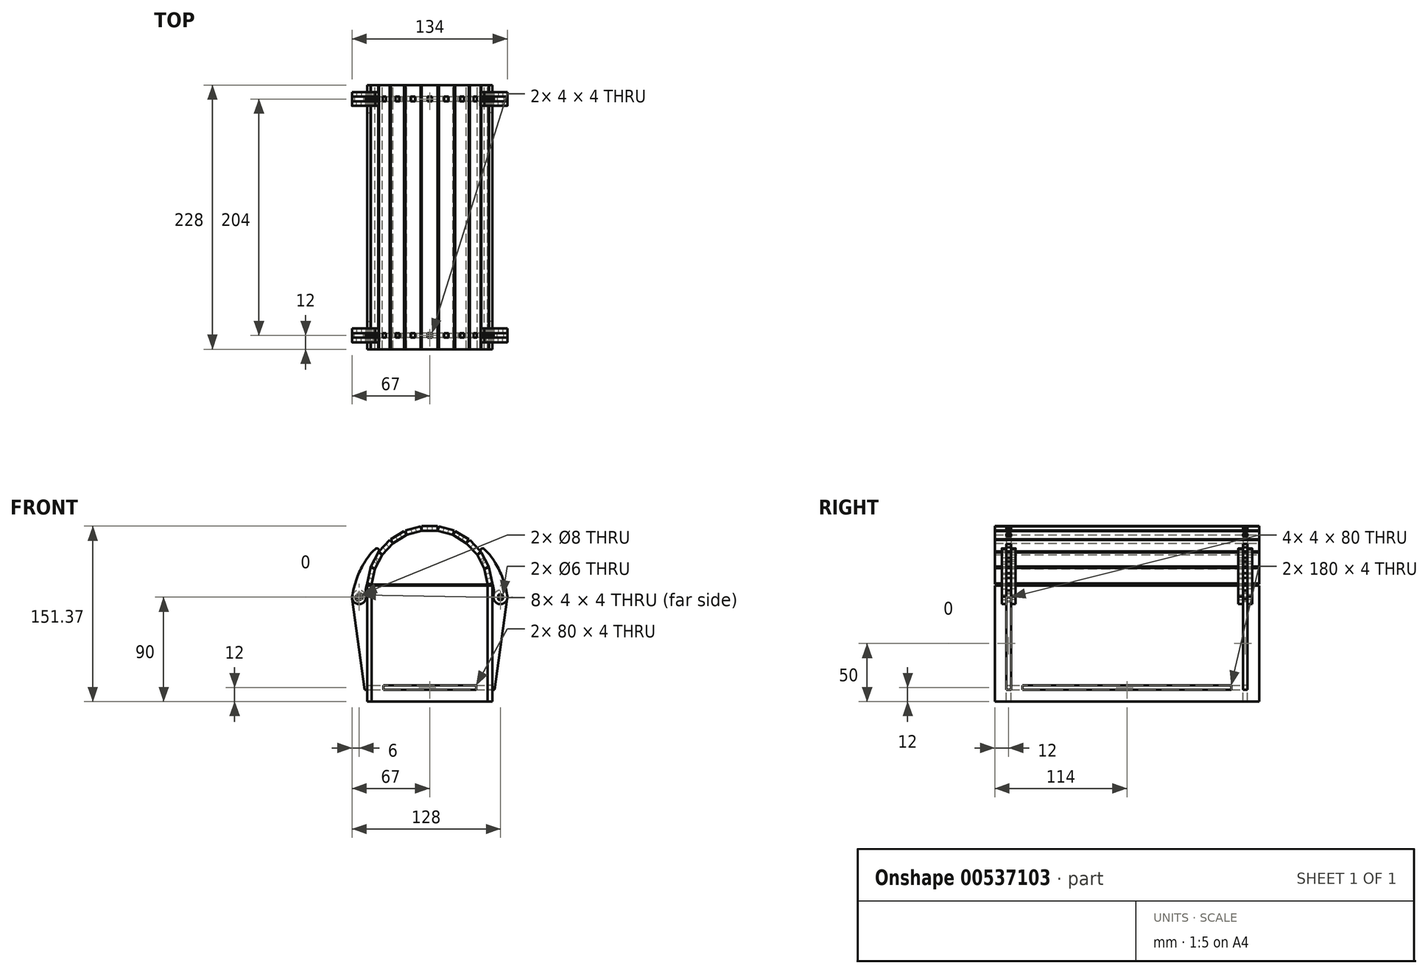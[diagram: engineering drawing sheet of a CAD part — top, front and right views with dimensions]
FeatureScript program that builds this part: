
annotation { "Feature Type Name" : "Feature", "Feature Type Description" : "" }
export const myFeature = defineFeature(function(context is Context, id is Id, definition is map)
    precondition{}
    {
        {
            var Q0;
            Q0=qCreatedBy(makeId("Front.planeOp"),FACE);
            cPlane(context, id + "F0", {"entities" : qUnion([Q0]), "cplaneType" : CPlaneType.OFFSET, "offset" : 100 * mm, "width" : 150 * mm, "height" : 150 * mm});
        }
        {
            var Q0;
            Q0=qCreatedBy(makeId("Front.planeOp"),FACE);
            cPlane(context, id + "F1", {"entities" : qUnion([Q0]), "cplaneType" : CPlaneType.OFFSET, "offset" : 100 * mm, "oppositeDirection" : true, "width" : 150 * mm, "height" : 150 * mm});
        }
        {
            var Q0;
            Q0=qCreatedBy(makeId("Right.planeOp"),FACE);
            cPlane(context, id + "F2", {"entities" : qUnion([Q0]), "cplaneType" : CPlaneType.OFFSET, "offset" : 50 * mm, "width" : 150 * mm, "height" : 150 * mm});
        }
        {
            var Q0;
            Q0=qCreatedBy(makeId("Right.planeOp"),FACE);
            cPlane(context, id + "F3", {"entities" : qUnion([Q0]), "cplaneType" : CPlaneType.OFFSET, "offset" : 50 * mm, "oppositeDirection" : true, "width" : 150 * mm, "height" : 150 * mm});
        }
        {
            var Q0;
            Q0=qCreatedBy(makeId("Top.planeOp"),FACE);
            cPlane(context, id + "F4", {"entities" : qUnion([Q0]), "cplaneType" : CPlaneType.OFFSET, "offset" : 40 * mm, "oppositeDirection" : true, "width" : 150 * mm, "height" : 150 * mm});
        }
        {
            var Q0;
            Q0=qCreatedBy(id+"F0.planeOp",FACE);
            var sketch = newSketch(context, id + "F5", { "sketchPlane" : qUnion([Q0])});
            skLineSegment(sketch, "E0.bottom", {"start": v(50, -50) * mm, "end": v(-50, -50) * mm});
            skLineSegment(sketch, "E0.top", {"start": v(50, 50) * mm, "end": v(-50, 50) * mm});
            skLineSegment(sketch, "E0.left", {"start": v(50, -50) * mm, "end": v(50, -40) * mm});
            skLineSegment(sketch, "E0.right", {"start": v(-50, -50) * mm, "end": v(-50, -40) * mm});
            skPoint(sketch, "E0.middle", {"position": v(0, 0) * mm});
            skLineSegment(sketch, "E1.bottom", {"start": v(-40, -36) * mm, "end": v(40, -36) * mm});
            skLineSegment(sketch, "E1.top", {"start": v(-40, -40) * mm, "end": v(40, -40) * mm});
            skLineSegment(sketch, "E1.left", {"start": v(-40, -36) * mm, "end": v(-40, -40) * mm});
            skLineSegment(sketch, "E1.right", {"start": v(40, -36) * mm, "end": v(40, -40) * mm});
            skLineSegment(sketch, "E2.bottom", {"start": v(-55, 40) * mm, "end": v(-50, 40) * mm});
            skLineSegment(sketch, "E2.top", {"start": v(-56, -40) * mm, "end": v(-50, -40) * mm});
            skLineSegment(sketch, "E3.trimOffspring", {"start": v(50, 40) * mm, "end": v(50, 50) * mm});
            skLineSegment(sketch, "E4.trimOffspring", {"start": v(-50, 40) * mm, "end": v(-50, 50) * mm});
            skPoint(sketch, "E5", {"position": v(0, 50) * mm});
            skLineSegment(sketch, "E6", {"start": v(-2, 97.37) * mm, "end": v(-2, 101.37) * mm});
            skLineSegment(sketch, "E7", {"start": v(-2, 101.37) * mm, "end": v(2, 101.37) * mm});
            skLineSegment(sketch, "E8", {"start": v(2, 101.37) * mm, "end": v(2, 97.37) * mm});
            skLineSegment(sketch, "E9", {"start": v(2, 97.37) * mm, "end": v(6.82, 97.37) * mm});
            skLineSegment(sketch, "E10", {"start": v(-2, 97.37) * mm, "end": v(-6.82, 97.37) * mm});
            skLineSegment(sketch, "E11.1.0", {"start": v(-12.54, 99.92) * mm, "end": v(-11.46, 96.07) * mm});
            skLineSegment(sketch, "E11.1.1", {"start": v(-16.4, 98.85) * mm, "end": v(-12.54, 99.92) * mm});
            skLineSegment(sketch, "E11.1.2", {"start": v(-15.31, 95) * mm, "end": v(-16.4, 98.85) * mm});
            skLineSegment(sketch, "E11.1.3", {"start": v(-15.31, 95) * mm, "end": v(-19.95, 93.7) * mm});
            skLineSegment(sketch, "E11.1.4", {"start": v(-11.46, 96.07) * mm, "end": v(-6.82, 97.37) * mm});
            skLineSegment(sketch, "E11.2.0", {"start": v(-26.15, 94.6) * mm, "end": v(-24.07, 91.19) * mm});
            skLineSegment(sketch, "E11.2.1", {"start": v(-29.57, 92.53) * mm, "end": v(-26.15, 94.6) * mm});
            skLineSegment(sketch, "E11.2.2", {"start": v(-27.49, 89.11) * mm, "end": v(-29.57, 92.53) * mm});
            skLineSegment(sketch, "E11.2.3", {"start": v(-27.49, 89.11) * mm, "end": v(-31.6, 86.6) * mm});
            skLineSegment(sketch, "E11.2.4", {"start": v(-24.07, 91.19) * mm, "end": v(-19.95, 93.7) * mm});
            skLineSegment(sketch, "E11.3.0", {"start": v(-37.82, 85.82) * mm, "end": v(-34.9, 83.08) * mm});
            skLineSegment(sketch, "E11.3.1", {"start": v(-40.55, 82.9) * mm, "end": v(-37.82, 85.82) * mm});
            skLineSegment(sketch, "E11.3.2", {"start": v(-37.62, 80.16) * mm, "end": v(-40.55, 82.9) * mm});
            skLineSegment(sketch, "E11.3.3", {"start": v(-37.62, 80.16) * mm, "end": v(-40.91, 76.64) * mm});
            skLineSegment(sketch, "E11.3.4", {"start": v(-34.9, 83.08) * mm, "end": v(-31.6, 86.6) * mm});
            skLineSegment(sketch, "E11.4.0", {"start": v(-46.68, 74.2) * mm, "end": v(-43.13, 72.36) * mm});
            skLineSegment(sketch, "E11.4.1", {"start": v(-48.52, 70.65) * mm, "end": v(-46.68, 74.2) * mm});
            skLineSegment(sketch, "E11.4.2", {"start": v(-44.97, 68.8) * mm, "end": v(-48.52, 70.65) * mm});
            skLineSegment(sketch, "E11.4.3", {"start": v(-44.97, 68.8) * mm, "end": v(-47.19, 64.53) * mm});
            skLineSegment(sketch, "E11.4.4", {"start": v(-43.13, 72.36) * mm, "end": v(-40.91, 76.64) * mm});
            skLineSegment(sketch, "E11.5.0", {"start": v(-52.09, 60.63) * mm, "end": v(-48.17, 59.81) * mm});
            skLineSegment(sketch, "E11.5.1", {"start": v(-52.9, 56.7) * mm, "end": v(-52.09, 60.63) * mm});
            skLineSegment(sketch, "E11.5.2", {"start": v(-48.98, 55.9) * mm, "end": v(-52.9, 56.7) * mm});
            skLineSegment(sketch, "E11.5.3", {"start": v(-48.98, 55.9) * mm, "end": v(-50, 51) * mm});
            skLineSegment(sketch, "E11.5.4", {"start": v(-48.17, 59.81) * mm, "end": v(-47.19, 64.53) * mm});
            skLineSegment(sketch, "E11.18.0", {"start": v(52.9, 56.7) * mm, "end": v(48.98, 55.9) * mm});
            skLineSegment(sketch, "E11.18.1", {"start": v(52.09, 60.63) * mm, "end": v(52.9, 56.7) * mm});
            skLineSegment(sketch, "E11.18.2", {"start": v(48.17, 59.81) * mm, "end": v(52.09, 60.63) * mm});
            skLineSegment(sketch, "E11.18.3", {"start": v(48.17, 59.81) * mm, "end": v(47.19, 64.53) * mm});
            skLineSegment(sketch, "E11.18.4", {"start": v(48.98, 55.9) * mm, "end": v(50, 51) * mm});
            skLineSegment(sketch, "E11.19.0", {"start": v(48.52, 70.65) * mm, "end": v(44.97, 68.8) * mm});
            skLineSegment(sketch, "E11.19.1", {"start": v(46.68, 74.2) * mm, "end": v(48.52, 70.65) * mm});
            skLineSegment(sketch, "E11.19.2", {"start": v(43.13, 72.36) * mm, "end": v(46.68, 74.2) * mm});
            skLineSegment(sketch, "E11.19.3", {"start": v(43.13, 72.36) * mm, "end": v(40.91, 76.64) * mm});
            skLineSegment(sketch, "E11.19.4", {"start": v(44.97, 68.8) * mm, "end": v(47.19, 64.53) * mm});
            skLineSegment(sketch, "E11.20.0", {"start": v(40.55, 82.9) * mm, "end": v(37.62, 80.16) * mm});
            skLineSegment(sketch, "E11.20.1", {"start": v(37.82, 85.82) * mm, "end": v(40.55, 82.9) * mm});
            skLineSegment(sketch, "E11.20.2", {"start": v(34.9, 83.08) * mm, "end": v(37.82, 85.82) * mm});
            skLineSegment(sketch, "E11.20.3", {"start": v(34.9, 83.08) * mm, "end": v(31.6, 86.6) * mm});
            skLineSegment(sketch, "E11.20.4", {"start": v(37.62, 80.16) * mm, "end": v(40.91, 76.64) * mm});
            skLineSegment(sketch, "E11.21.0", {"start": v(29.57, 92.53) * mm, "end": v(27.49, 89.11) * mm});
            skLineSegment(sketch, "E11.21.1", {"start": v(26.15, 94.6) * mm, "end": v(29.57, 92.53) * mm});
            skLineSegment(sketch, "E11.21.2", {"start": v(24.07, 91.19) * mm, "end": v(26.15, 94.6) * mm});
            skLineSegment(sketch, "E11.21.3", {"start": v(24.07, 91.19) * mm, "end": v(19.95, 93.7) * mm});
            skLineSegment(sketch, "E11.21.4", {"start": v(27.49, 89.11) * mm, "end": v(31.6, 86.6) * mm});
            skLineSegment(sketch, "E11.22.0", {"start": v(16.4, 98.85) * mm, "end": v(15.31, 95) * mm});
            skLineSegment(sketch, "E11.22.1", {"start": v(12.54, 99.92) * mm, "end": v(16.4, 98.85) * mm});
            skLineSegment(sketch, "E11.22.2", {"start": v(11.46, 96.07) * mm, "end": v(12.54, 99.92) * mm});
            skLineSegment(sketch, "E11.22.3", {"start": v(11.46, 96.07) * mm, "end": v(6.82, 97.37) * mm});
            skLineSegment(sketch, "E11.22.4", {"start": v(15.31, 95) * mm, "end": v(19.95, 93.7) * mm});
            skLineSegment(sketch, "E12", {"start": v(50, 51) * mm, "end": v(-50, 51) * mm});
            skCircle(sketch, "E13", {"center": v(-61, 40) * mm, "radius": 4 * mm});
            skArc(sketch, "E14", {"start": v(-55, 40) * mm, "mid": v(-61.09, 46) * mm, "end": v(-67, 39.83) * mm});
            skLineSegment(sketch, "E15", {"start": v(-67, 39.83) * mm, "end": v(-56, -40) * mm});
            skPoint(sketch, "E16.end.orphan", {"position": v(-57, 40) * mm});
            skLineSegment(sketch, "E17.MirrorCS", {"start": v(67, 39.83) * mm, "end": v(56, -40) * mm});
            skLineSegment(sketch, "E18.MirrorCS", {"start": v(55, 40) * mm, "end": v(50, 40) * mm});
            skArc(sketch, "E19.MirrorCS", {"start": v(55, 40) * mm, "mid": v(61.09, 46) * mm, "end": v(67, 39.83) * mm});
            skLineSegment(sketch, "E20", {"start": v(40, -40) * mm, "end": v(56, -40) * mm});
            skCircle(sketch, "E21", {"center": v(61, 40) * mm, "radius": 3 * mm});
            skSolve(sketch);
        }
        {
            var Q0;
            Q0 = qSketchRegion(id + "F5", true);
            extrude(context, id + "F6", {"entities" : qUnion([Q0]), "depth" : 4 * mm, "offsetDistance" : 25 * mm});
        }
        {
            var Q0;
            Q0=qCreatedBy(id+"F1.planeOp",FACE);
            var sketch = newSketch(context, id + "F7", { "sketchPlane" : qUnion([Q0])});
            skLineSegment(sketch, "E22.bottom", {"start": v(50, -50) * mm, "end": v(-50, -50) * mm});
            skLineSegment(sketch, "E22.top", {"start": v(50, 50) * mm, "end": v(-50, 50) * mm});
            skLineSegment(sketch, "E22.left", {"start": v(50, -50) * mm, "end": v(50, -40) * mm});
            skLineSegment(sketch, "E22.right", {"start": v(-50, -50) * mm, "end": v(-50, -40) * mm});
            skPoint(sketch, "E22.middle", {"position": v(0, 0) * mm});
            skLineSegment(sketch, "E23.bottom", {"start": v(-40, -36) * mm, "end": v(40, -36) * mm});
            skLineSegment(sketch, "E23.top", {"start": v(-40, -40) * mm, "end": v(40, -40) * mm});
            skLineSegment(sketch, "E23.left", {"start": v(-40, -36) * mm, "end": v(-40, -40) * mm});
            skLineSegment(sketch, "E23.right", {"start": v(40, -36) * mm, "end": v(40, -40) * mm});
            skLineSegment(sketch, "E24.top", {"start": v(-56, -40) * mm, "end": v(-50, -40) * mm});
            skLineSegment(sketch, "E25.trimOffspring", {"start": v(50, 40) * mm, "end": v(50, 50) * mm});
            skLineSegment(sketch, "E26.trimOffspring", {"start": v(-50, 40) * mm, "end": v(-50, 50) * mm});
            skLineSegment(sketch, "E27.bottom", {"start": v(-55, 40) * mm, "end": v(-50, 40) * mm});
            skCircle(sketch, "E28", {"center": v(-61, 40) * mm, "radius": 4 * mm});
            skArc(sketch, "E29", {"start": v(-55, 40) * mm, "mid": v(-61.73, 45.95) * mm, "end": v(-66.82, 38.54) * mm});
            skLineSegment(sketch, "E30", {"start": v(-67, 39.83) * mm, "end": v(-56, -40) * mm});
            skLineSegment(sketch, "E31.MirrorCS", {"start": v(55, 40) * mm, "end": v(50, 40) * mm});
            skArc(sketch, "E32.MirrorCS", {"start": v(55, 40) * mm, "mid": v(61.73, 45.95) * mm, "end": v(66.82, 38.54) * mm});
            skLineSegment(sketch, "E33.MirrorCS", {"start": v(67, 39.83) * mm, "end": v(56, -40) * mm});
            skLineSegment(sketch, "E34.MirrorCS", {"start": v(56, -40) * mm, "end": v(50, -40) * mm});
            skCircle(sketch, "E35", {"center": v(61, 40) * mm, "radius": 3 * mm});
            skSolve(sketch);
        }
        {
            var Q0;
            Q0 = qSketchRegion(id + "F7", true);
            extrude(context, id + "F8", {"entities" : qUnion([Q0]), "oppositeDirection" : true, "depth" : 4 * mm, "offsetDistance" : 25 * mm});
        }
        {
            var Q0;
            Q0=qCreatedBy(id+"F2.planeOp",FACE);
            var sketch = newSketch(context, id + "F9", { "sketchPlane" : qUnion([Q0])});
            skLineSegment(sketch, "E36.bottom", {"start": v(-114, 50) * mm, "end": v(114, 50) * mm});
            skLineSegment(sketch, "E36.top", {"start": v(-114, -50) * mm, "end": v(114, -50) * mm});
            skLineSegment(sketch, "E36.left", {"start": v(-114, 50) * mm, "end": v(-114, -50) * mm});
            skLineSegment(sketch, "E36.right", {"start": v(114, 50) * mm, "end": v(114, -50) * mm});
            skPoint(sketch, "E36.middle", {"position": v(0, 0) * mm});
            skLineSegment(sketch, "E37.bottom", {"start": v(-104, 40) * mm, "end": v(-100, 40) * mm});
            skLineSegment(sketch, "E37.top", {"start": v(-104, -40) * mm, "end": v(-100, -40) * mm});
            skLineSegment(sketch, "E37.left", {"start": v(-104, 40) * mm, "end": v(-104, -40) * mm});
            skLineSegment(sketch, "E37.right", {"start": v(-100, 40) * mm, "end": v(-100, -40) * mm});
            skLineSegment(sketch, "E38.MirrorCS", {"start": v(104, -40) * mm, "end": v(100, -40) * mm});
            skLineSegment(sketch, "E39.MirrorCS", {"start": v(104, 40) * mm, "end": v(100, 40) * mm});
            skLineSegment(sketch, "E40.MirrorCS", {"start": v(100, 40) * mm, "end": v(100, -40) * mm});
            skLineSegment(sketch, "E41.MirrorCS", {"start": v(104, 40) * mm, "end": v(104, -40) * mm});
            skLineSegment(sketch, "E42.bottom", {"start": v(-90, -36) * mm, "end": v(90, -36) * mm});
            skLineSegment(sketch, "E42.top", {"start": v(-90, -40) * mm, "end": v(90, -40) * mm});
            skLineSegment(sketch, "E42.left", {"start": v(-90, -36) * mm, "end": v(-90, -40) * mm});
            skLineSegment(sketch, "E42.right", {"start": v(90, -36) * mm, "end": v(90, -40) * mm});
            skSolve(sketch);
        }
        {
            var Q0;
            Q0 = qSketchRegion(id + "F9", true);
            extrude(context, id + "F10", {"entities" : qUnion([Q0]), "depth" : 4 * mm, "offsetDistance" : 25 * mm});
        }
        {
            var Q0;
            Q0=qCreatedBy(id+"F3.planeOp",FACE);
            var sketch = newSketch(context, id + "F11", { "sketchPlane" : qUnion([Q0])});
            skLineSegment(sketch, "E43.bottom", {"start": v(-114, 50) * mm, "end": v(114, 50) * mm});
            skLineSegment(sketch, "E43.top", {"start": v(-114, -50) * mm, "end": v(114, -50) * mm});
            skLineSegment(sketch, "E43.left", {"start": v(-114, 50) * mm, "end": v(-114, -50) * mm});
            skLineSegment(sketch, "E43.right", {"start": v(114, 50) * mm, "end": v(114, -50) * mm});
            skPoint(sketch, "E43.middle", {"position": v(0, 0) * mm});
            skLineSegment(sketch, "E44.bottom", {"start": v(-104, 40) * mm, "end": v(-100, 40) * mm});
            skLineSegment(sketch, "E44.top", {"start": v(-104, -40) * mm, "end": v(-100, -40) * mm});
            skLineSegment(sketch, "E44.left", {"start": v(-104, 40) * mm, "end": v(-104, -40) * mm});
            skLineSegment(sketch, "E44.right", {"start": v(-100, 40) * mm, "end": v(-100, -40) * mm});
            skLineSegment(sketch, "E45.MirrorCS", {"start": v(104, -40) * mm, "end": v(100, -40) * mm});
            skLineSegment(sketch, "E46.MirrorCS", {"start": v(104, 40) * mm, "end": v(100, 40) * mm});
            skLineSegment(sketch, "E47.MirrorCS", {"start": v(100, 40) * mm, "end": v(100, -40) * mm});
            skLineSegment(sketch, "E48.MirrorCS", {"start": v(104, 40) * mm, "end": v(104, -40) * mm});
            skLineSegment(sketch, "E49.bottom", {"start": v(-90, -36) * mm, "end": v(90, -36) * mm});
            skLineSegment(sketch, "E49.top", {"start": v(-90, -40) * mm, "end": v(90, -40) * mm});
            skLineSegment(sketch, "E49.left", {"start": v(-90, -36) * mm, "end": v(-90, -40) * mm});
            skLineSegment(sketch, "E49.right", {"start": v(90, -36) * mm, "end": v(90, -40) * mm});
            skSolve(sketch);
        }
        {
            var Q0;
            Q0 = qSketchRegion(id + "F11", true);
            extrude(context, id + "F12", {"entities" : qUnion([Q0]), "oppositeDirection" : true, "depth" : 4 * mm, "offsetDistance" : 25 * mm});
        }
        {
            var Q0;
            Q0=qCreatedBy(id+"F4.planeOp",FACE);
            var sketch = newSketch(context, id + "F13", { "sketchPlane" : qUnion([Q0])});
            skLineSegment(sketch, "E50.bottom", {"start": v(-50, -100) * mm, "end": v(-40, -100) * mm});
            skLineSegment(sketch, "E50.top", {"start": v(-50, 100) * mm, "end": v(-40, 100) * mm});
            skLineSegment(sketch, "E50.left", {"start": v(-50, -100) * mm, "end": v(-50, -90) * mm});
            skLineSegment(sketch, "E50.right", {"start": v(50, -100) * mm, "end": v(50, -90) * mm});
            skPoint(sketch, "E50.middle", {"position": v(0, 0) * mm});
            skLineSegment(sketch, "E51.bottom", {"start": v(-54, -90) * mm, "end": v(-50, -90) * mm});
            skLineSegment(sketch, "E51.top", {"start": v(-54, 90) * mm, "end": v(-50, 90) * mm});
            skLineSegment(sketch, "E51.left", {"start": v(-54, -90) * mm, "end": v(-54, 90) * mm});
            skLineSegment(sketch, "E52.trimOffspring", {"start": v(-50, 90) * mm, "end": v(-50, 100) * mm});
            skLineSegment(sketch, "E53.MirrorCS", {"start": v(54, 90) * mm, "end": v(50, 90) * mm});
            skLineSegment(sketch, "E54.MirrorCS", {"start": v(54, -90) * mm, "end": v(50, -90) * mm});
            skLineSegment(sketch, "E55.MirrorCS", {"start": v(54, -90) * mm, "end": v(54, 90) * mm});
            skLineSegment(sketch, "E56.trimOffspring", {"start": v(50, 90) * mm, "end": v(50, 100) * mm});
            skLineSegment(sketch, "E57.bottom", {"start": v(40, -104) * mm, "end": v(-40, -104) * mm});
            skLineSegment(sketch, "E57.left", {"start": v(40, -104) * mm, "end": v(40, -100) * mm});
            skLineSegment(sketch, "E57.right", {"start": v(-40, -104) * mm, "end": v(-40, -100) * mm});
            skLineSegment(sketch, "E58", {"start": v(0, 0) * mm, "end": v(13.37, 0) * mm});
            skLineSegment(sketch, "E59.MirrorCS", {"start": v(-40, 104) * mm, "end": v(-40, 100) * mm});
            skLineSegment(sketch, "E60.MirrorCS", {"start": v(40, 104) * mm, "end": v(40, 100) * mm});
            skLineSegment(sketch, "E61.MirrorCS", {"start": v(40, 104) * mm, "end": v(-40, 104) * mm});
            skLineSegment(sketch, "E62.trimOffspring", {"start": v(40, -100) * mm, "end": v(50, -100) * mm});
            skLineSegment(sketch, "E63.trimOffspring", {"start": v(40, 100) * mm, "end": v(50, 100) * mm});
            skSolve(sketch);
        }
        {
            var Q0;
            Q0 = qSketchRegion(id + "F13", true);
            extrude(context, id + "F14", {"entities" : qUnion([Q0]), "depth" : 4 * mm, "offsetDistance" : 25 * mm});
        }
        {
            var Q0;
            Q0=makeQuery(id+"F6.opExtrude","SWEPT_BODY",BODY,{"disambiguationData":[OSD([sQuery(id+"F5.wireOp",EDGE,"E6"),sQuery(id+"F5.wireOp",EDGE,"E7"),sQuery(id+"F5.wireOp",EDGE,"E8"),sQuery(id+"F5.wireOp",EDGE,"E9"),sQuery(id+"F5.wireOp",EDGE,"E10"),sQuery(id+"F5.wireOp",EDGE,"E11.1.0"),sQuery(id+"F5.wireOp",EDGE,"E11.1.1"),sQuery(id+"F5.wireOp",EDGE,"E11.1.2"),sQuery(id+"F5.wireOp",EDGE,"E11.1.3"),sQuery(id+"F5.wireOp",EDGE,"E11.1.4"),sQuery(id+"F5.wireOp",EDGE,"E11.2.0"),sQuery(id+"F5.wireOp",EDGE,"E11.2.1"),sQuery(id+"F5.wireOp",EDGE,"E11.2.2"),sQuery(id+"F5.wireOp",EDGE,"E11.2.3"),sQuery(id+"F5.wireOp",EDGE,"E11.2.4"),sQuery(id+"F5.wireOp",EDGE,"E11.3.0"),sQuery(id+"F5.wireOp",EDGE,"E11.3.1"),sQuery(id+"F5.wireOp",EDGE,"E11.3.2"),sQuery(id+"F5.wireOp",EDGE,"E11.3.3"),sQuery(id+"F5.wireOp",EDGE,"E11.3.4"),sQuery(id+"F5.wireOp",EDGE,"E11.4.0"),sQuery(id+"F5.wireOp",EDGE,"E11.4.1"),sQuery(id+"F5.wireOp",EDGE,"E11.4.2"),sQuery(id+"F5.wireOp",EDGE,"E11.4.3"),sQuery(id+"F5.wireOp",EDGE,"E11.4.4"),sQuery(id+"F5.wireOp",EDGE,"E11.5.0"),sQuery(id+"F5.wireOp",EDGE,"E11.5.1"),sQuery(id+"F5.wireOp",EDGE,"E11.5.2"),sQuery(id+"F5.wireOp",EDGE,"E11.5.3"),sQuery(id+"F5.wireOp",EDGE,"E11.5.4"),sQuery(id+"F5.wireOp",EDGE,"E11.18.0"),sQuery(id+"F5.wireOp",EDGE,"E11.18.1"),sQuery(id+"F5.wireOp",EDGE,"E11.18.2"),sQuery(id+"F5.wireOp",EDGE,"E11.18.3"),sQuery(id+"F5.wireOp",EDGE,"E11.18.4"),sQuery(id+"F5.wireOp",EDGE,"E11.19.0"),sQuery(id+"F5.wireOp",EDGE,"E11.19.1"),sQuery(id+"F5.wireOp",EDGE,"E11.19.2"),sQuery(id+"F5.wireOp",EDGE,"E11.19.3"),sQuery(id+"F5.wireOp",EDGE,"E11.19.4"),sQuery(id+"F5.wireOp",EDGE,"E11.20.0"),sQuery(id+"F5.wireOp",EDGE,"E11.20.1"),sQuery(id+"F5.wireOp",EDGE,"E11.20.2"),sQuery(id+"F5.wireOp",EDGE,"E11.20.3"),sQuery(id+"F5.wireOp",EDGE,"E11.20.4"),sQuery(id+"F5.wireOp",EDGE,"E11.21.0"),sQuery(id+"F5.wireOp",EDGE,"E11.21.1"),sQuery(id+"F5.wireOp",EDGE,"E11.21.2"),sQuery(id+"F5.wireOp",EDGE,"E11.21.3"),sQuery(id+"F5.wireOp",EDGE,"E11.21.4"),sQuery(id+"F5.wireOp",EDGE,"E11.22.0"),sQuery(id+"F5.wireOp",EDGE,"E11.22.1"),sQuery(id+"F5.wireOp",EDGE,"E11.22.2"),sQuery(id+"F5.wireOp",EDGE,"E11.22.3"),sQuery(id+"F5.wireOp",EDGE,"E11.22.4"),sQuery(id+"F5.wireOp",EDGE,"E12")])]});
            var Q1;
            Q1=qCreatedBy(makeId("Front.planeOp"),FACE);
            mirror(context, id + "F15", {"entities" : qUnion([Q0]), "mirrorPlane" : qUnion([Q1])});
        }
        {
            var Q0;
            Q0=makeQuery(id+"F6.opExtrude","SWEPT_FACE",FACE,{"disambiguationData":[OSD([sQuery(id+"F5.wireOp",EDGE,"E9")])]});
            cPlane(context, id + "F16", {"entities" : qUnion([Q0]), "cplaneType" : CPlaneType.OFFSET, "offset" : 0 * mm, "width" : 150 * mm, "height" : 150 * mm});
        }
        {
            var Q0;
            Q0=qCreatedBy(id+"F16.planeOp",FACE);
            var sketch = newSketch(context, id + "F17", { "sketchPlane" : qUnion([Q0])});
            skLineSegment(sketch, "E64", {"start": v(-6.82, -114) * mm, "end": v(-6.82, 114) * mm});
            skLineSegment(sketch, "E65", {"start": v(6.82, -114) * mm, "end": v(6.82, 114) * mm});
            skLineSegment(sketch, "E66", {"start": v(-6.82, -114) * mm, "end": v(6.82, -114) * mm});
            skLineSegment(sketch, "E67.bottom", {"start": v(-2, -100) * mm, "end": v(2, -100) * mm});
            skLineSegment(sketch, "E67.top", {"start": v(-2, -104) * mm, "end": v(2, -104) * mm});
            skLineSegment(sketch, "E67.left", {"start": v(-2, -100) * mm, "end": v(-2, -104) * mm});
            skLineSegment(sketch, "E67.right", {"start": v(2, -100) * mm, "end": v(2, -104) * mm});
            skLineSegment(sketch, "E68.MirrorCS", {"start": v(-6.82, 114) * mm, "end": v(6.82, 114) * mm});
            skLineSegment(sketch, "E69.MirrorCS", {"start": v(2, 100) * mm, "end": v(2, 104) * mm});
            skLineSegment(sketch, "E70.MirrorCS", {"start": v(-2, 100) * mm, "end": v(2, 100) * mm});
            skLineSegment(sketch, "E71.MirrorCS", {"start": v(-2, 104) * mm, "end": v(2, 104) * mm});
            skLineSegment(sketch, "E72.MirrorCS", {"start": v(-2, 100) * mm, "end": v(-2, 104) * mm});
            skSolve(sketch);
        }
        {
            var Q0;
            Q0 = qSketchRegion(id + "F17", true);
            extrude(context, id + "F18", {"entities" : qUnion([Q0]), "depth" : 4 * mm, "offsetDistance" : 25 * mm});
        }
        {
            var Q0;
            Q0=makeQuery(id+"F6.opExtrude","SWEPT_FACE",FACE,{"disambiguationData":[OSD([sQuery(id+"F5.wireOp",EDGE,"E11.22.4")])]});
            cPlane(context, id + "F19", {"entities" : qUnion([Q0]), "cplaneType" : CPlaneType.OFFSET, "offset" : 0 * mm, "width" : 150 * mm, "height" : 150 * mm});
        }
        {
            var Q0;
            Q0=qCreatedBy(id+"F19.planeOp",FACE);
            var sketch = newSketch(context, id + "F20", { "sketchPlane" : qUnion([Q0])});
            skLineSegment(sketch, "E73", {"start": v(-19.7, -114) * mm, "end": v(-19.7, 114) * mm});
            skLineSegment(sketch, "E74", {"start": v(-6.07, -114) * mm, "end": v(-6.07, 114) * mm});
            skLineSegment(sketch, "E75", {"start": v(-19.7, -114) * mm, "end": v(-6.07, -114) * mm});
            skLineSegment(sketch, "E76.bottom", {"start": v(-14.89, -100) * mm, "end": v(-10.89, -100) * mm});
            skLineSegment(sketch, "E76.top", {"start": v(-14.89, -104) * mm, "end": v(-10.89, -104) * mm});
            skLineSegment(sketch, "E76.left", {"start": v(-14.89, -100) * mm, "end": v(-14.89, -104) * mm});
            skLineSegment(sketch, "E76.right", {"start": v(-10.89, -100) * mm, "end": v(-10.89, -104) * mm});
            skLineSegment(sketch, "E77.MirrorCS", {"start": v(-19.7, 114) * mm, "end": v(-6.07, 114) * mm});
            skLineSegment(sketch, "E78.MirrorCS", {"start": v(-10.89, 100) * mm, "end": v(-10.89, 104) * mm});
            skLineSegment(sketch, "E79.MirrorCS", {"start": v(-14.89, 100) * mm, "end": v(-10.89, 100) * mm});
            skLineSegment(sketch, "E80.MirrorCS", {"start": v(-14.89, 104) * mm, "end": v(-10.89, 104) * mm});
            skLineSegment(sketch, "E81.MirrorCS", {"start": v(-14.89, 100) * mm, "end": v(-14.89, 104) * mm});
            skSolve(sketch);
        }
        {
            var Q0;
            Q0 = qSketchRegion(id + "F20", true);
            extrude(context, id + "F21", {"entities" : qUnion([Q0]), "depth" : 4 * mm, "offsetDistance" : 25 * mm});
        }
        {
            var Q0;
            Q0=makeQuery(id+"F6.opExtrude","SWEPT_FACE",FACE,{"disambiguationData":[OSD([sQuery(id+"F5.wireOp",EDGE,"E11.21.4")])]});
            var sketch = newSketch(context, id + "F22", { "sketchPlane" : qUnion([Q0])});
            skLineSegment(sketch, "E82", {"start": v(-31.63, -114) * mm, "end": v(-31.63, 114) * mm});
            skLineSegment(sketch, "E83", {"start": v(-18, -114) * mm, "end": v(-18, 114) * mm});
            skLineSegment(sketch, "E84", {"start": v(-31.63, -114) * mm, "end": v(-18, -114) * mm});
            skLineSegment(sketch, "E85.bottom", {"start": v(-26.82, -100) * mm, "end": v(-22.82, -100) * mm});
            skLineSegment(sketch, "E85.top", {"start": v(-26.82, -104) * mm, "end": v(-22.82, -104) * mm});
            skLineSegment(sketch, "E85.left", {"start": v(-26.82, -100) * mm, "end": v(-26.82, -104) * mm});
            skLineSegment(sketch, "E85.right", {"start": v(-22.82, -100) * mm, "end": v(-22.82, -104) * mm});
            skLineSegment(sketch, "E86.MirrorCS", {"start": v(-31.63, 114) * mm, "end": v(-18, 114) * mm});
            skLineSegment(sketch, "E87.MirrorCS", {"start": v(-22.82, 100) * mm, "end": v(-22.82, 104) * mm});
            skLineSegment(sketch, "E88.MirrorCS", {"start": v(-26.82, 100) * mm, "end": v(-22.82, 100) * mm});
            skLineSegment(sketch, "E89.MirrorCS", {"start": v(-26.82, 104) * mm, "end": v(-22.82, 104) * mm});
            skLineSegment(sketch, "E90.MirrorCS", {"start": v(-26.82, 100) * mm, "end": v(-26.82, 104) * mm});
            skSolve(sketch);
        }
        {
            var Q0;
            Q0 = qSketchRegion(id + "F22", true);
            extrude(context, id + "F23", {"entities" : qUnion([Q0]), "depth" : 4 * mm, "offsetDistance" : 25 * mm});
        }
        {
            var Q0;
            Q0=makeQuery(id+"F6.opExtrude","SWEPT_FACE",FACE,{"disambiguationData":[OSD([sQuery(id+"F5.wireOp",EDGE,"E11.1.3")])]});
            var sketch = newSketch(context, id + "F24", { "sketchPlane" : qUnion([Q0])});
            skLineSegment(sketch, "E91", {"start": v(6.07, -114) * mm, "end": v(6.07, 114) * mm});
            skLineSegment(sketch, "E92", {"start": v(19.7, -114) * mm, "end": v(19.7, 114) * mm});
            skLineSegment(sketch, "E93", {"start": v(6.07, -114) * mm, "end": v(19.7, -114) * mm});
            skLineSegment(sketch, "E94.bottom", {"start": v(10.89, -100) * mm, "end": v(14.89, -100) * mm});
            skLineSegment(sketch, "E94.top", {"start": v(10.89, -104) * mm, "end": v(14.89, -104) * mm});
            skLineSegment(sketch, "E94.left", {"start": v(10.89, -100) * mm, "end": v(10.89, -104) * mm});
            skLineSegment(sketch, "E94.right", {"start": v(14.89, -100) * mm, "end": v(14.89, -104) * mm});
            skLineSegment(sketch, "E95.MirrorCS", {"start": v(6.07, 114) * mm, "end": v(19.7, 114) * mm});
            skLineSegment(sketch, "E96.MirrorCS", {"start": v(14.89, 100) * mm, "end": v(14.89, 104) * mm});
            skLineSegment(sketch, "E97.MirrorCS", {"start": v(10.89, 100) * mm, "end": v(14.89, 100) * mm});
            skLineSegment(sketch, "E98.MirrorCS", {"start": v(10.89, 104) * mm, "end": v(14.89, 104) * mm});
            skLineSegment(sketch, "E99.MirrorCS", {"start": v(10.89, 100) * mm, "end": v(10.89, 104) * mm});
            skSolve(sketch);
        }
        {
            var Q0;
            Q0 = qSketchRegion(id + "F24", true);
            extrude(context, id + "F25", {"entities" : qUnion([Q0]), "depth" : 4 * mm, "offsetDistance" : 25 * mm});
        }
        {
            var Q0;
            Q0=makeQuery(id+"F6.opExtrude","SWEPT_FACE",FACE,{"disambiguationData":[OSD([sQuery(id+"F5.wireOp",EDGE,"E11.2.3")])]});
            var sketch = newSketch(context, id + "F26", { "sketchPlane" : qUnion([Q0])});
            skLineSegment(sketch, "E100", {"start": v(18, -114) * mm, "end": v(18, 114) * mm});
            skLineSegment(sketch, "E101", {"start": v(31.63, -114) * mm, "end": v(31.63, 114) * mm});
            skLineSegment(sketch, "E102", {"start": v(18, -114) * mm, "end": v(31.63, -114) * mm});
            skLineSegment(sketch, "E103.bottom", {"start": v(22.82, -100) * mm, "end": v(26.82, -100) * mm});
            skLineSegment(sketch, "E103.top", {"start": v(22.82, -104) * mm, "end": v(26.82, -104) * mm});
            skLineSegment(sketch, "E103.left", {"start": v(22.82, -100) * mm, "end": v(22.82, -104) * mm});
            skLineSegment(sketch, "E103.right", {"start": v(26.82, -100) * mm, "end": v(26.82, -104) * mm});
            skLineSegment(sketch, "E104.MirrorCS", {"start": v(18, 114) * mm, "end": v(31.63, 114) * mm});
            skLineSegment(sketch, "E105.MirrorCS", {"start": v(26.82, 100) * mm, "end": v(26.82, 104) * mm});
            skLineSegment(sketch, "E106.MirrorCS", {"start": v(22.82, 100) * mm, "end": v(26.82, 100) * mm});
            skLineSegment(sketch, "E107.MirrorCS", {"start": v(22.82, 104) * mm, "end": v(26.82, 104) * mm});
            skLineSegment(sketch, "E108.MirrorCS", {"start": v(22.82, 100) * mm, "end": v(22.82, 104) * mm});
            skSolve(sketch);
        }
        {
            var Q0;
            Q0 = qSketchRegion(id + "F26", true);
            extrude(context, id + "F27", {"entities" : qUnion([Q0]), "depth" : 4 * mm, "offsetDistance" : 25 * mm});
        }
        {
            var Q0;
            Q0=makeQuery(id+"F6.opExtrude","SWEPT_FACE",FACE,{"disambiguationData":[OSD([sQuery(id+"F5.wireOp",EDGE,"E11.3.3")])]});
            var sketch = newSketch(context, id + "F28", { "sketchPlane" : qUnion([Q0])});
            skLineSegment(sketch, "E109", {"start": v(114, 28.09) * mm, "end": v(-114, 28.09) * mm});
            skLineSegment(sketch, "E110", {"start": v(114, 41.72) * mm, "end": v(-114, 41.72) * mm});
            skLineSegment(sketch, "E111", {"start": v(114, 28.09) * mm, "end": v(114, 41.72) * mm});
            skLineSegment(sketch, "E112.bottom", {"start": v(100, 32.9) * mm, "end": v(100, 36.9) * mm});
            skLineSegment(sketch, "E112.top", {"start": v(104, 32.9) * mm, "end": v(104, 36.9) * mm});
            skLineSegment(sketch, "E112.left", {"start": v(100, 32.9) * mm, "end": v(104, 32.9) * mm});
            skLineSegment(sketch, "E112.right", {"start": v(100, 36.9) * mm, "end": v(104, 36.9) * mm});
            skLineSegment(sketch, "E113.MirrorCS", {"start": v(-114, 28.09) * mm, "end": v(-114, 41.72) * mm});
            skLineSegment(sketch, "E114.MirrorCS", {"start": v(-100, 36.9) * mm, "end": v(-104, 36.9) * mm});
            skLineSegment(sketch, "E115.MirrorCS", {"start": v(-100, 32.9) * mm, "end": v(-100, 36.9) * mm});
            skLineSegment(sketch, "E116.MirrorCS", {"start": v(-104, 32.9) * mm, "end": v(-104, 36.9) * mm});
            skLineSegment(sketch, "E117.MirrorCS", {"start": v(-100, 32.9) * mm, "end": v(-104, 32.9) * mm});
            skSolve(sketch);
        }
        {
            var Q0;
            Q0 = qSketchRegion(id + "F28", true);
            extrude(context, id + "F29", {"entities" : qUnion([Q0]), "depth" : 4 * mm, "offsetDistance" : 25 * mm});
        }
        {
            var Q0;
            Q0=makeQuery(id+"F6.opExtrude","SWEPT_FACE",FACE,{"disambiguationData":[OSD([sQuery(id+"F5.wireOp",EDGE,"E11.4.3")])]});
            var sketch = newSketch(context, id + "F30", { "sketchPlane" : qUnion([Q0])});
            skLineSegment(sketch, "E118", {"start": v(114, 35.59) * mm, "end": v(-114, 35.59) * mm});
            skLineSegment(sketch, "E119", {"start": v(114, 49.22) * mm, "end": v(-114, 49.22) * mm});
            skLineSegment(sketch, "E120", {"start": v(114, 35.59) * mm, "end": v(114, 49.22) * mm});
            skLineSegment(sketch, "E121.bottom", {"start": v(100, 40.4) * mm, "end": v(100, 44.4) * mm});
            skLineSegment(sketch, "E121.top", {"start": v(108, 40.4) * mm, "end": v(108, 44.4) * mm});
            skLineSegment(sketch, "E121.left", {"start": v(100, 40.4) * mm, "end": v(108, 40.4) * mm});
            skLineSegment(sketch, "E121.right", {"start": v(100, 44.4) * mm, "end": v(108, 44.4) * mm});
            skLineSegment(sketch, "E122.MirrorCS", {"start": v(-114, 35.59) * mm, "end": v(-114, 49.22) * mm});
            skLineSegment(sketch, "E123.MirrorCS", {"start": v(-100, 44.4) * mm, "end": v(-108, 44.4) * mm});
            skLineSegment(sketch, "E124.MirrorCS", {"start": v(-100, 40.4) * mm, "end": v(-100, 44.4) * mm});
            skLineSegment(sketch, "E125.MirrorCS", {"start": v(-108, 40.4) * mm, "end": v(-108, 44.4) * mm});
            skLineSegment(sketch, "E126.MirrorCS", {"start": v(-100, 40.4) * mm, "end": v(-108, 40.4) * mm});
            skSolve(sketch);
        }
        {
            var Q0;
            Q0 = qSketchRegion(id + "F30", true);
            extrude(context, id + "F31", {"entities" : qUnion([Q0]), "depth" : 4 * mm, "offsetDistance" : 25 * mm});
        }
        {
            var Q0;
            Q0=makeQuery(id+"F6.opExtrude","SWEPT_FACE",FACE,{"disambiguationData":[OSD([sQuery(id+"F5.wireOp",EDGE,"E11.5.3")])]});
            var sketch = newSketch(context, id + "F32", { "sketchPlane" : qUnion([Q0])});
            skLineSegment(sketch, "E127", {"start": v(114, 39.94) * mm, "end": v(-114, 39.94) * mm});
            skLineSegment(sketch, "E128", {"start": v(114, 53.58) * mm, "end": v(-114, 53.58) * mm});
            skLineSegment(sketch, "E129", {"start": v(114, 39.94) * mm, "end": v(114, 53.58) * mm});
            skLineSegment(sketch, "E130.bottom", {"start": v(96, 44.76) * mm, "end": v(96, 48.76) * mm});
            skLineSegment(sketch, "E130.top", {"start": v(108, 44.76) * mm, "end": v(108, 48.76) * mm});
            skLineSegment(sketch, "E130.left", {"start": v(96, 44.76) * mm, "end": v(108, 44.76) * mm});
            skLineSegment(sketch, "E130.right", {"start": v(96, 48.76) * mm, "end": v(108, 48.76) * mm});
            skLineSegment(sketch, "E131.MirrorCS", {"start": v(-114, 39.94) * mm, "end": v(-114, 53.58) * mm});
            skLineSegment(sketch, "E132.bottom", {"start": v(-108, 48.76) * mm, "end": v(-96, 48.76) * mm});
            skLineSegment(sketch, "E132.top", {"start": v(-108, 44.76) * mm, "end": v(-96, 44.76) * mm});
            skLineSegment(sketch, "E132.left", {"start": v(-108, 48.76) * mm, "end": v(-108, 44.76) * mm});
            skLineSegment(sketch, "E132.right", {"start": v(-96, 48.76) * mm, "end": v(-96, 44.76) * mm});
            skSolve(sketch);
        }
        {
            var Q0;
            Q0 = qSketchRegion(id + "F32", true);
            extrude(context, id + "F33", {"entities" : qUnion([Q0]), "depth" : 4 * mm, "offsetDistance" : 25 * mm});
        }
        {
            var Q0;
            Q0=makeQuery(id+"F6.opExtrude","SWEPT_FACE",FACE,{"disambiguationData":[OSD([sQuery(id+"F5.wireOp",EDGE,"E11.20.4")])]});
            var sketch = newSketch(context, id + "F34", { "sketchPlane" : qUnion([Q0])});
            skLineSegment(sketch, "E133", {"start": v(-114, 41.72) * mm, "end": v(114, 41.72) * mm});
            skLineSegment(sketch, "E134", {"start": v(-114, 28.09) * mm, "end": v(114, 28.09) * mm});
            skLineSegment(sketch, "E135", {"start": v(-114, 41.72) * mm, "end": v(-114, 28.09) * mm});
            skLineSegment(sketch, "E136.bottom", {"start": v(-100, 36.9) * mm, "end": v(-100, 32.9) * mm});
            skLineSegment(sketch, "E136.top", {"start": v(-104, 36.9) * mm, "end": v(-104, 32.9) * mm});
            skLineSegment(sketch, "E136.left", {"start": v(-100, 36.9) * mm, "end": v(-104, 36.9) * mm});
            skLineSegment(sketch, "E136.right", {"start": v(-100, 32.9) * mm, "end": v(-104, 32.9) * mm});
            skLineSegment(sketch, "E137.MirrorCS", {"start": v(114, 41.72) * mm, "end": v(114, 28.09) * mm});
            skLineSegment(sketch, "E138.MirrorCS", {"start": v(100, 32.9) * mm, "end": v(104, 32.9) * mm});
            skLineSegment(sketch, "E139.MirrorCS", {"start": v(100, 36.9) * mm, "end": v(100, 32.9) * mm});
            skLineSegment(sketch, "E140.MirrorCS", {"start": v(104, 36.9) * mm, "end": v(104, 32.9) * mm});
            skLineSegment(sketch, "E141.MirrorCS", {"start": v(100, 36.9) * mm, "end": v(104, 36.9) * mm});
            skSolve(sketch);
        }
        {
            var Q0;
            Q0 = qSketchRegion(id + "F34", true);
            extrude(context, id + "F35", {"entities" : qUnion([Q0]), "depth" : 4 * mm, "offsetDistance" : 25 * mm});
        }
        {
            var Q0;
            Q0=makeQuery(id+"F6.opExtrude","SWEPT_FACE",FACE,{"disambiguationData":[OSD([sQuery(id+"F5.wireOp",EDGE,"E11.19.4")])]});
            var sketch = newSketch(context, id + "F36", { "sketchPlane" : qUnion([Q0])});
            skLineSegment(sketch, "E142", {"start": v(-114, 49.22) * mm, "end": v(114, 49.22) * mm});
            skLineSegment(sketch, "E143", {"start": v(-114, 35.59) * mm, "end": v(114, 35.59) * mm});
            skLineSegment(sketch, "E144", {"start": v(-114, 49.22) * mm, "end": v(-114, 35.59) * mm});
            skLineSegment(sketch, "E145.bottom", {"start": v(-96, 44.4) * mm, "end": v(-96, 40.4) * mm});
            skLineSegment(sketch, "E145.top", {"start": v(-108, 44.4) * mm, "end": v(-108, 40.4) * mm});
            skLineSegment(sketch, "E145.left", {"start": v(-96, 44.4) * mm, "end": v(-108, 44.4) * mm});
            skLineSegment(sketch, "E145.right", {"start": v(-96, 40.4) * mm, "end": v(-108, 40.4) * mm});
            skLineSegment(sketch, "E146.MirrorCS", {"start": v(114, 49.22) * mm, "end": v(114, 35.59) * mm});
            skLineSegment(sketch, "E147.MirrorCS", {"start": v(96, 40.4) * mm, "end": v(108, 40.4) * mm});
            skLineSegment(sketch, "E148.MirrorCS", {"start": v(96, 44.4) * mm, "end": v(108, 44.4) * mm});
            skLineSegment(sketch, "E149.MirrorCS", {"start": v(96, 44.4) * mm, "end": v(96, 40.4) * mm});
            skLineSegment(sketch, "E150.MirrorCS", {"start": v(108, 44.4) * mm, "end": v(108, 40.4) * mm});
            skSolve(sketch);
        }
        {
            var Q0;
            Q0 = qSketchRegion(id + "F36", true);
            extrude(context, id + "F37", {"entities" : qUnion([Q0]), "depth" : 4 * mm, "offsetDistance" : 25 * mm});
        }
        {
            var Q0;
            Q0=makeQuery(id+"F6.opExtrude","SWEPT_FACE",FACE,{"disambiguationData":[OSD([sQuery(id+"F5.wireOp",EDGE,"E11.18.4")])]});
            var sketch = newSketch(context, id + "F38", { "sketchPlane" : qUnion([Q0])});
            skLineSegment(sketch, "E151", {"start": v(-114, 53.58) * mm, "end": v(114, 53.58) * mm});
            skLineSegment(sketch, "E152", {"start": v(-114, 39.94) * mm, "end": v(114, 39.94) * mm});
            skLineSegment(sketch, "E153", {"start": v(-114, 53.58) * mm, "end": v(-114, 39.94) * mm});
            skLineSegment(sketch, "E154.bottom", {"start": v(-96, 48.76) * mm, "end": v(-96, 44.76) * mm});
            skLineSegment(sketch, "E154.top", {"start": v(-108, 48.76) * mm, "end": v(-108, 44.76) * mm});
            skLineSegment(sketch, "E154.right", {"start": v(-96, 44.76) * mm, "end": v(-108, 44.76) * mm});
            skLineSegment(sketch, "E155.MirrorCS", {"start": v(114, 53.58) * mm, "end": v(114, 39.94) * mm});
            skLineSegment(sketch, "E156.MirrorCS", {"start": v(96, 44.76) * mm, "end": v(108, 44.76) * mm});
            skLineSegment(sketch, "E157.MirrorCS", {"start": v(108, 48.76) * mm, "end": v(108, 44.76) * mm});
            skLineSegment(sketch, "E158.MirrorCS", {"start": v(96, 48.76) * mm, "end": v(96, 44.76) * mm});
            skLineSegment(sketch, "E159", {"start": v(-108, 48.76) * mm, "end": v(-96, 48.76) * mm});
            skLineSegment(sketch, "E160", {"start": v(96, 48.76) * mm, "end": v(108, 48.76) * mm});
            skSolve(sketch);
        }
        {
            var Q0;
            Q0 = qSketchRegion(id + "F38", true);
            extrude(context, id + "F39", {"entities" : qUnion([Q0]), "depth" : 4 * mm, "offsetDistance" : 25 * mm});
        }
        {
            var Q0;
            Q0=makeQuery(id+"F6.opExtrude","CAP_FACE",FACE,{"disambiguationData":[OSD([sQuery(id+"F5.wireOp",EDGE,"E6"),sQuery(id+"F5.wireOp",EDGE,"E7"),sQuery(id+"F5.wireOp",EDGE,"E8"),sQuery(id+"F5.wireOp",EDGE,"E9"),sQuery(id+"F5.wireOp",EDGE,"E10"),sQuery(id+"F5.wireOp",EDGE,"E11.1.0"),sQuery(id+"F5.wireOp",EDGE,"E11.1.1"),sQuery(id+"F5.wireOp",EDGE,"E11.1.2"),sQuery(id+"F5.wireOp",EDGE,"E11.1.3"),sQuery(id+"F5.wireOp",EDGE,"E11.1.4"),sQuery(id+"F5.wireOp",EDGE,"E11.2.0"),sQuery(id+"F5.wireOp",EDGE,"E11.2.1"),sQuery(id+"F5.wireOp",EDGE,"E11.2.2"),sQuery(id+"F5.wireOp",EDGE,"E11.2.3"),sQuery(id+"F5.wireOp",EDGE,"E11.2.4"),sQuery(id+"F5.wireOp",EDGE,"E11.3.0"),sQuery(id+"F5.wireOp",EDGE,"E11.3.1"),sQuery(id+"F5.wireOp",EDGE,"E11.3.2"),sQuery(id+"F5.wireOp",EDGE,"E11.3.3"),sQuery(id+"F5.wireOp",EDGE,"E11.3.4"),sQuery(id+"F5.wireOp",EDGE,"E11.4.0"),sQuery(id+"F5.wireOp",EDGE,"E11.4.1"),sQuery(id+"F5.wireOp",EDGE,"E11.4.2"),sQuery(id+"F5.wireOp",EDGE,"E11.4.3"),sQuery(id+"F5.wireOp",EDGE,"E11.4.4"),sQuery(id+"F5.wireOp",EDGE,"E11.5.0"),sQuery(id+"F5.wireOp",EDGE,"E11.5.1"),sQuery(id+"F5.wireOp",EDGE,"E11.5.2"),sQuery(id+"F5.wireOp",EDGE,"E11.5.3"),sQuery(id+"F5.wireOp",EDGE,"E11.5.4"),sQuery(id+"F5.wireOp",EDGE,"E11.18.0"),sQuery(id+"F5.wireOp",EDGE,"E11.18.1"),sQuery(id+"F5.wireOp",EDGE,"E11.18.2"),sQuery(id+"F5.wireOp",EDGE,"E11.18.3"),sQuery(id+"F5.wireOp",EDGE,"E11.18.4"),sQuery(id+"F5.wireOp",EDGE,"E11.19.0"),sQuery(id+"F5.wireOp",EDGE,"E11.19.1"),sQuery(id+"F5.wireOp",EDGE,"E11.19.2"),sQuery(id+"F5.wireOp",EDGE,"E11.19.3"),sQuery(id+"F5.wireOp",EDGE,"E11.19.4"),sQuery(id+"F5.wireOp",EDGE,"E11.20.0"),sQuery(id+"F5.wireOp",EDGE,"E11.20.1"),sQuery(id+"F5.wireOp",EDGE,"E11.20.2"),sQuery(id+"F5.wireOp",EDGE,"E11.20.3"),sQuery(id+"F5.wireOp",EDGE,"E11.20.4"),sQuery(id+"F5.wireOp",EDGE,"E11.21.0"),sQuery(id+"F5.wireOp",EDGE,"E11.21.1"),sQuery(id+"F5.wireOp",EDGE,"E11.21.2"),sQuery(id+"F5.wireOp",EDGE,"E11.21.3"),sQuery(id+"F5.wireOp",EDGE,"E11.21.4"),sQuery(id+"F5.wireOp",EDGE,"E11.22.0"),sQuery(id+"F5.wireOp",EDGE,"E11.22.1"),sQuery(id+"F5.wireOp",EDGE,"E11.22.2"),sQuery(id+"F5.wireOp",EDGE,"E11.22.3"),sQuery(id+"F5.wireOp",EDGE,"E11.22.4"),sQuery(id+"F5.wireOp",EDGE,"E12")])],"isStart":false});
            var sketch = newSketch(context, id + "F40", { "sketchPlane" : qUnion([Q0])});
            skCircle(sketch, "E161", {"center": v(-61, 40) * mm, "radius": 6 * mm});
            skLineSegment(sketch, "E162", {"start": v(-44.97, 68.8) * mm, "end": v(-48.52, 70.65) * mm});
            skLineSegment(sketch, "E163", {"start": v(-48.52, 70.65) * mm, "end": v(-51, 65.88) * mm});
            skLineSegment(sketch, "E164", {"start": v(-46.68, 74.2) * mm, "end": v(-43.97, 79.43) * mm});
            skArc(sketch, "E165.filletArc", {"start": v(-43.97, 79.43) * mm, "mid": v(-44.61, 81.85) * mm, "end": v(-47.09, 81.45) * mm});
            skLineSegment(sketch, "E166", {"start": v(-52.09, 60.63) * mm, "end": v(-51, 65.88) * mm});
            skLineSegment(sketch, "E167", {"start": v(-52.09, 60.63) * mm, "end": v(-48.17, 59.81) * mm});
            skLineSegment(sketch, "E168", {"start": v(-48.17, 59.81) * mm, "end": v(-48.98, 55.9) * mm});
            skLineSegment(sketch, "E169", {"start": v(-48.98, 55.9) * mm, "end": v(-52.9, 56.7) * mm});
            skLineSegment(sketch, "E170", {"start": v(-52.9, 56.7) * mm, "end": v(-53.88, 52) * mm});
            skLineSegment(sketch, "E171", {"start": v(-55, 39.89) * mm, "end": v(-55, 40.11) * mm});
            skLineSegment(sketch, "E172", {"start": v(-55, 40.11) * mm, "end": v(-55.13, 46.97) * mm});
            skFitSpline(sketch, "E173", {"points": [v(-53.88, 52) * mm, v(-54.53, 50.17) * mm, v(-55.13, 46.97) * mm, v(-55.13, 46.8) * mm, v(-55.13, 46.8) * mm], "startDerivative": vector(-1.69, -3.88) * mm, "endDerivative": vector(0, -0.06) * mm});
            skFitSpline(sketch, "E174", {"points": [v(-47.09, 81.45) * mm, v(-57.91, 67.12) * mm, v(-63.05, 55.7) * mm, v(-66.99, 40.35) * mm], "startDerivative": vector(-40.09, -32.55) * mm, "endDerivative": vector(-2.37, -33.03) * mm});
            skLineSegment(sketch, "E175.bottom", {"start": v(-63, 42) * mm, "end": v(-59, 42) * mm});
            skLineSegment(sketch, "E175.top", {"start": v(-63, 38) * mm, "end": v(-59, 38) * mm});
            skLineSegment(sketch, "E175.left", {"start": v(-63, 42) * mm, "end": v(-63, 38) * mm});
            skLineSegment(sketch, "E175.right", {"start": v(-59, 42) * mm, "end": v(-59, 38) * mm});
            skLineSegment(sketch, "E176", {"start": v(-46.68, 74.2) * mm, "end": v(-44.97, 68.8) * mm});
            skSolve(sketch);
        }
        {
            var Q0;
            Q0 = qSketchRegion(id + "F40", true);
            extrude(context, id + "F41", {"entities" : qUnion([Q0]), "depth" : 4 * mm, "offsetDistance" : 25 * mm});
        }
        {
            var Q0;
            Q0=makeQuery(id+"F41.opExtrude","SWEPT_BODY",BODY,{"disambiguationData":[OSD([sQuery(id+"F40.wireOp",EDGE,"E161"),sQuery(id+"F40.wireOp",EDGE,"t4tbokRh-8WQ7-ktuR-oRIJ-KhsfdOefVWlQ"),sQuery(id+"F40.wireOp",EDGE,"BNBL1Nzf-ZYxI-rDMI-PRVd-LXwGIi5Q9C7N"),sQuery(id+"F40.wireOp",EDGE,"E162"),sQuery(id+"F40.wireOp",EDGE,"E163"),sQuery(id+"F40.wireOp",EDGE,"E164"),sQuery(id+"F40.wireOp",EDGE,"E165.filletArc"),sQuery(id+"F40.wireOp",EDGE,"E166"),sQuery(id+"F40.wireOp",EDGE,"E167"),sQuery(id+"F40.wireOp",EDGE,"E168"),sQuery(id+"F40.wireOp",EDGE,"E169"),sQuery(id+"F40.wireOp",EDGE,"E170"),sQuery(id+"F40.wireOp",EDGE,"E172"),sQuery(id+"F40.wireOp",EDGE,"E173"),sQuery(id+"F40.wireOp",EDGE,"E174"),sQuery(id+"F40.wireOp",EDGE,"E175.bottom"),sQuery(id+"F40.wireOp",EDGE,"E175.top"),sQuery(id+"F40.wireOp",EDGE,"E175.left"),sQuery(id+"F40.wireOp",EDGE,"E175.right")])]});
            var Q1;
            Q1=qCreatedBy(makeId("Front.planeOp"),FACE);
            mirror(context, id + "F42", {"entities" : qUnion([Q0]), "mirrorPlane" : qUnion([Q1])});
        }
        {
            var Q0;
            Q0=makeQuery(id+"F41.opExtrude","SWEPT_BODY",BODY,{"disambiguationData":[OSD([sQuery(id+"F40.wireOp",EDGE,"E161"),sQuery(id+"F40.wireOp",EDGE,"t4tbokRh-8WQ7-ktuR-oRIJ-KhsfdOefVWlQ"),sQuery(id+"F40.wireOp",EDGE,"BNBL1Nzf-ZYxI-rDMI-PRVd-LXwGIi5Q9C7N"),sQuery(id+"F40.wireOp",EDGE,"E162"),sQuery(id+"F40.wireOp",EDGE,"E163"),sQuery(id+"F40.wireOp",EDGE,"E164"),sQuery(id+"F40.wireOp",EDGE,"E165.filletArc"),sQuery(id+"F40.wireOp",EDGE,"E166"),sQuery(id+"F40.wireOp",EDGE,"E167"),sQuery(id+"F40.wireOp",EDGE,"E168"),sQuery(id+"F40.wireOp",EDGE,"E169"),sQuery(id+"F40.wireOp",EDGE,"E170"),sQuery(id+"F40.wireOp",EDGE,"E172"),sQuery(id+"F40.wireOp",EDGE,"E173"),sQuery(id+"F40.wireOp",EDGE,"E174"),sQuery(id+"F40.wireOp",EDGE,"E175.bottom"),sQuery(id+"F40.wireOp",EDGE,"E175.top"),sQuery(id+"F40.wireOp",EDGE,"E175.left"),sQuery(id+"F40.wireOp",EDGE,"E175.right")])]});
            var Q1;
            Q1=qCreatedBy(id+"F0.planeOp",FACE);
            mirror(context, id + "F43", {"entities" : qUnion([Q0]), "mirrorPlane" : qUnion([Q1])});
        }
        {
            var Q0;
            Q0=makeQuery(id+"F43.opPattern","COPY",BODY,{"derivedFrom":makeQuery(id+"F41.opExtrude","SWEPT_BODY",BODY,{"disambiguationData":[OSD([sQuery(id+"F40.wireOp",EDGE,"E161"),sQuery(id+"F40.wireOp",EDGE,"t4tbokRh-8WQ7-ktuR-oRIJ-KhsfdOefVWlQ"),sQuery(id+"F40.wireOp",EDGE,"BNBL1Nzf-ZYxI-rDMI-PRVd-LXwGIi5Q9C7N"),sQuery(id+"F40.wireOp",EDGE,"E162"),sQuery(id+"F40.wireOp",EDGE,"E163"),sQuery(id+"F40.wireOp",EDGE,"E164"),sQuery(id+"F40.wireOp",EDGE,"E165.filletArc"),sQuery(id+"F40.wireOp",EDGE,"E166"),sQuery(id+"F40.wireOp",EDGE,"E167"),sQuery(id+"F40.wireOp",EDGE,"E168"),sQuery(id+"F40.wireOp",EDGE,"E169"),sQuery(id+"F40.wireOp",EDGE,"E170"),sQuery(id+"F40.wireOp",EDGE,"E172"),sQuery(id+"F40.wireOp",EDGE,"E173"),sQuery(id+"F40.wireOp",EDGE,"E174"),sQuery(id+"F40.wireOp",EDGE,"E175.bottom"),sQuery(id+"F40.wireOp",EDGE,"E175.top"),sQuery(id+"F40.wireOp",EDGE,"E175.left"),sQuery(id+"F40.wireOp",EDGE,"E175.right")])]}),"instanceName":"1"});
            transform(context, id + "F44", {"entities" : qUnion([Q0]), "transformType" : TransformType.TRANSLATION_3D, "dx" : 0 * mm, "dy" : -4 * mm, "dz" : 0 * mm, "makeCopy" : false});
        }
        {
            var Q0;
            Q0=makeQuery(id+"F43.opPattern","COPY",BODY,{"derivedFrom":makeQuery(id+"F41.opExtrude","SWEPT_BODY",BODY,{"disambiguationData":[OSD([sQuery(id+"F40.wireOp",EDGE,"E161"),sQuery(id+"F40.wireOp",EDGE,"t4tbokRh-8WQ7-ktuR-oRIJ-KhsfdOefVWlQ"),sQuery(id+"F40.wireOp",EDGE,"BNBL1Nzf-ZYxI-rDMI-PRVd-LXwGIi5Q9C7N"),sQuery(id+"F40.wireOp",EDGE,"E162"),sQuery(id+"F40.wireOp",EDGE,"E163"),sQuery(id+"F40.wireOp",EDGE,"E164"),sQuery(id+"F40.wireOp",EDGE,"E165.filletArc"),sQuery(id+"F40.wireOp",EDGE,"E166"),sQuery(id+"F40.wireOp",EDGE,"E167"),sQuery(id+"F40.wireOp",EDGE,"E168"),sQuery(id+"F40.wireOp",EDGE,"E169"),sQuery(id+"F40.wireOp",EDGE,"E170"),sQuery(id+"F40.wireOp",EDGE,"E172"),sQuery(id+"F40.wireOp",EDGE,"E173"),sQuery(id+"F40.wireOp",EDGE,"E174"),sQuery(id+"F40.wireOp",EDGE,"E175.bottom"),sQuery(id+"F40.wireOp",EDGE,"E175.top"),sQuery(id+"F40.wireOp",EDGE,"E175.left"),sQuery(id+"F40.wireOp",EDGE,"E175.right")])]}),"instanceName":"1"});
            var Q1;
            Q1=qCreatedBy(makeId("Front.planeOp"),FACE);
            mirror(context, id + "F45", {"entities" : qUnion([Q0]), "mirrorPlane" : qUnion([Q1])});
        }
        {
            var Q0;
            Q0=makeQuery(id+"F41.opExtrude","SWEPT_BODY",BODY,{"disambiguationData":[OSD([sQuery(id+"F40.wireOp",EDGE,"E161"),sQuery(id+"F40.wireOp",EDGE,"t4tbokRh-8WQ7-ktuR-oRIJ-KhsfdOefVWlQ"),sQuery(id+"F40.wireOp",EDGE,"BNBL1Nzf-ZYxI-rDMI-PRVd-LXwGIi5Q9C7N"),sQuery(id+"F40.wireOp",EDGE,"E162"),sQuery(id+"F40.wireOp",EDGE,"E163"),sQuery(id+"F40.wireOp",EDGE,"E164"),sQuery(id+"F40.wireOp",EDGE,"E165.filletArc"),sQuery(id+"F40.wireOp",EDGE,"E166"),sQuery(id+"F40.wireOp",EDGE,"E167"),sQuery(id+"F40.wireOp",EDGE,"E168"),sQuery(id+"F40.wireOp",EDGE,"E169"),sQuery(id+"F40.wireOp",EDGE,"E170"),sQuery(id+"F40.wireOp",EDGE,"E172"),sQuery(id+"F40.wireOp",EDGE,"E173"),sQuery(id+"F40.wireOp",EDGE,"E174"),sQuery(id+"F40.wireOp",EDGE,"E175.bottom"),sQuery(id+"F40.wireOp",EDGE,"E175.top"),sQuery(id+"F40.wireOp",EDGE,"E175.left"),sQuery(id+"F40.wireOp",EDGE,"E175.right")])]});
            var Q1;
            Q1=makeQuery(id+"F43.opPattern","COPY",BODY,{"derivedFrom":makeQuery(id+"F41.opExtrude","SWEPT_BODY",BODY,{"disambiguationData":[OSD([sQuery(id+"F40.wireOp",EDGE,"E161"),sQuery(id+"F40.wireOp",EDGE,"t4tbokRh-8WQ7-ktuR-oRIJ-KhsfdOefVWlQ"),sQuery(id+"F40.wireOp",EDGE,"BNBL1Nzf-ZYxI-rDMI-PRVd-LXwGIi5Q9C7N"),sQuery(id+"F40.wireOp",EDGE,"E162"),sQuery(id+"F40.wireOp",EDGE,"E163"),sQuery(id+"F40.wireOp",EDGE,"E164"),sQuery(id+"F40.wireOp",EDGE,"E165.filletArc"),sQuery(id+"F40.wireOp",EDGE,"E166"),sQuery(id+"F40.wireOp",EDGE,"E167"),sQuery(id+"F40.wireOp",EDGE,"E168"),sQuery(id+"F40.wireOp",EDGE,"E169"),sQuery(id+"F40.wireOp",EDGE,"E170"),sQuery(id+"F40.wireOp",EDGE,"E172"),sQuery(id+"F40.wireOp",EDGE,"E173"),sQuery(id+"F40.wireOp",EDGE,"E174"),sQuery(id+"F40.wireOp",EDGE,"E175.bottom"),sQuery(id+"F40.wireOp",EDGE,"E175.top"),sQuery(id+"F40.wireOp",EDGE,"E175.left"),sQuery(id+"F40.wireOp",EDGE,"E175.right")])]}),"instanceName":"1"});
            var Q2;
            Q2=qCreatedBy(makeId("Right.planeOp"),FACE);
            mirror(context, id + "F46", {"entities" : qUnion([Q0, Q1]), "mirrorPlane" : qUnion([Q2])});
        }
        {
            var Q0;
            Q0=makeQuery(id+"F46.opPattern","COPY",BODY,{"derivedFrom":makeQuery(id+"F43.opPattern","COPY",BODY,{"derivedFrom":makeQuery(id+"F41.opExtrude","SWEPT_BODY",BODY,{"disambiguationData":[OSD([sQuery(id+"F40.wireOp",EDGE,"E161"),sQuery(id+"F40.wireOp",EDGE,"t4tbokRh-8WQ7-ktuR-oRIJ-KhsfdOefVWlQ"),sQuery(id+"F40.wireOp",EDGE,"BNBL1Nzf-ZYxI-rDMI-PRVd-LXwGIi5Q9C7N"),sQuery(id+"F40.wireOp",EDGE,"E162"),sQuery(id+"F40.wireOp",EDGE,"E163"),sQuery(id+"F40.wireOp",EDGE,"E164"),sQuery(id+"F40.wireOp",EDGE,"E165.filletArc"),sQuery(id+"F40.wireOp",EDGE,"E166"),sQuery(id+"F40.wireOp",EDGE,"E167"),sQuery(id+"F40.wireOp",EDGE,"E168"),sQuery(id+"F40.wireOp",EDGE,"E169"),sQuery(id+"F40.wireOp",EDGE,"E170"),sQuery(id+"F40.wireOp",EDGE,"E172"),sQuery(id+"F40.wireOp",EDGE,"E173"),sQuery(id+"F40.wireOp",EDGE,"E174"),sQuery(id+"F40.wireOp",EDGE,"E175.bottom"),sQuery(id+"F40.wireOp",EDGE,"E175.top"),sQuery(id+"F40.wireOp",EDGE,"E175.left"),sQuery(id+"F40.wireOp",EDGE,"E175.right")])]}),"instanceName":"1"}),"instanceName":"1"});
            var Q1;
            Q1=makeQuery(id+"F46.opPattern","COPY",BODY,{"derivedFrom":makeQuery(id+"F41.opExtrude","SWEPT_BODY",BODY,{"disambiguationData":[OSD([sQuery(id+"F40.wireOp",EDGE,"E161"),sQuery(id+"F40.wireOp",EDGE,"t4tbokRh-8WQ7-ktuR-oRIJ-KhsfdOefVWlQ"),sQuery(id+"F40.wireOp",EDGE,"BNBL1Nzf-ZYxI-rDMI-PRVd-LXwGIi5Q9C7N"),sQuery(id+"F40.wireOp",EDGE,"E162"),sQuery(id+"F40.wireOp",EDGE,"E163"),sQuery(id+"F40.wireOp",EDGE,"E164"),sQuery(id+"F40.wireOp",EDGE,"E165.filletArc"),sQuery(id+"F40.wireOp",EDGE,"E166"),sQuery(id+"F40.wireOp",EDGE,"E167"),sQuery(id+"F40.wireOp",EDGE,"E168"),sQuery(id+"F40.wireOp",EDGE,"E169"),sQuery(id+"F40.wireOp",EDGE,"E170"),sQuery(id+"F40.wireOp",EDGE,"E172"),sQuery(id+"F40.wireOp",EDGE,"E173"),sQuery(id+"F40.wireOp",EDGE,"E174"),sQuery(id+"F40.wireOp",EDGE,"E175.bottom"),sQuery(id+"F40.wireOp",EDGE,"E175.top"),sQuery(id+"F40.wireOp",EDGE,"E175.left"),sQuery(id+"F40.wireOp",EDGE,"E175.right")])]}),"instanceName":"1"});
            var Q2;
            Q2=qCreatedBy(makeId("Front.planeOp"),FACE);
            mirror(context, id + "F47", {"entities" : qUnion([Q0, Q1]), "mirrorPlane" : qUnion([Q2])});
        }
    });
